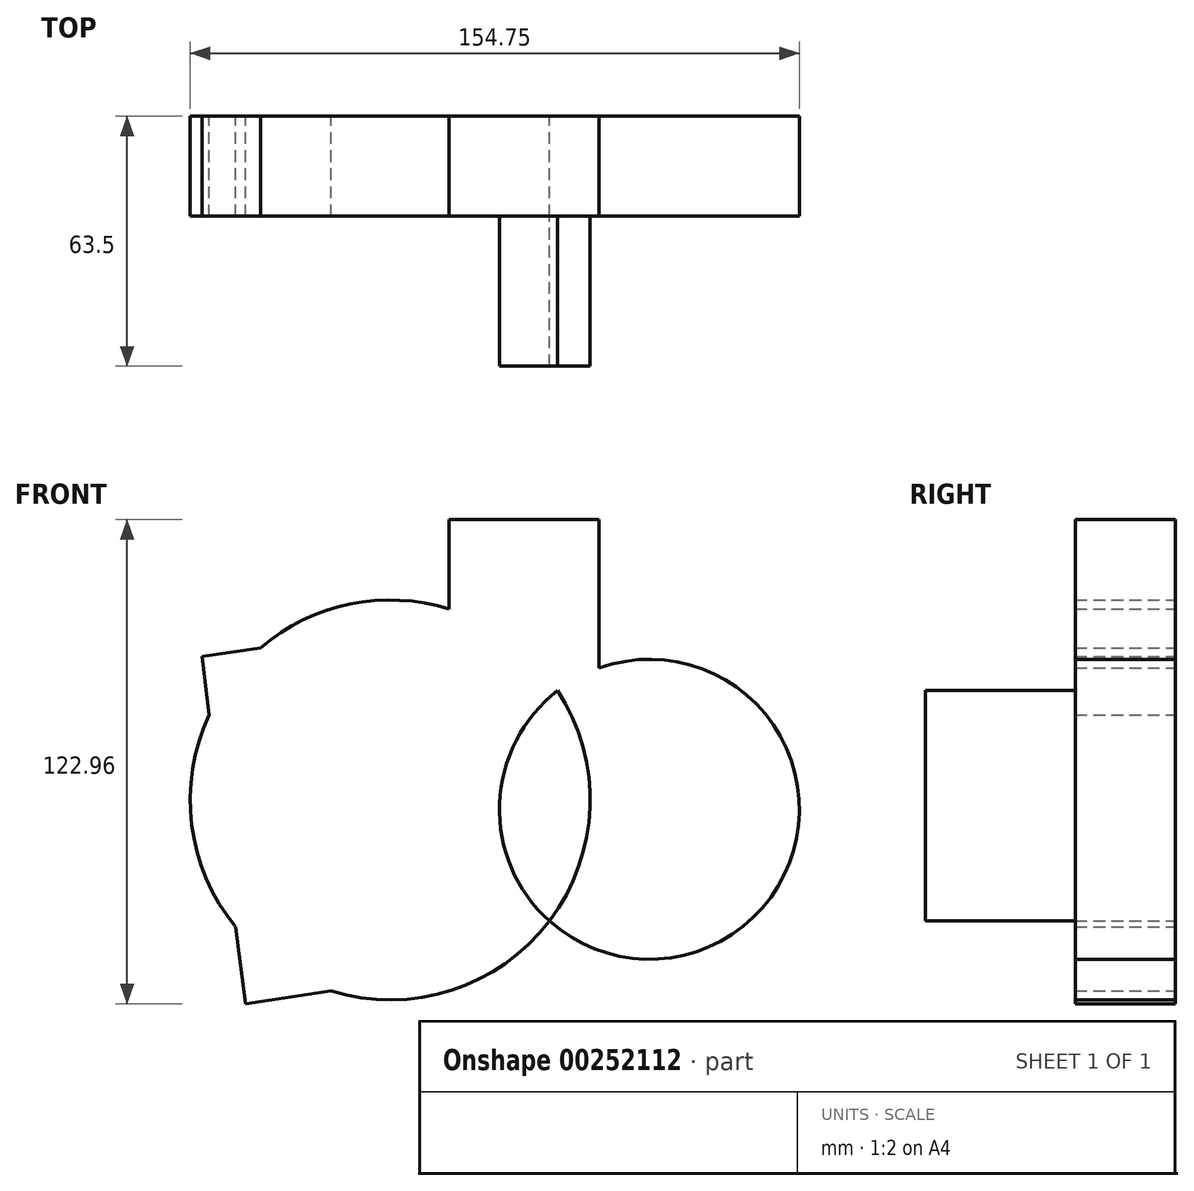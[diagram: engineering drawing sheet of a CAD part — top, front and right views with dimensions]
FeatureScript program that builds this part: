
annotation { "Feature Type Name" : "Feature", "Feature Type Description" : "" }
export const myFeature = defineFeature(function(context is Context, id is Id, definition is map)
    precondition{}
    {
        {
            var Q0;
            Q0=qCreatedBy(makeId("Front.planeOp"),FACE);
            var sketch = newSketch(context, id + "F0", { "sketchPlane" : qUnion([Q0])});
            skCircle(sketch, "E0", {"center": v(0, 0) * mm, "radius": 38.1 * mm});
            skLineSegment(sketch, "E1", {"start": v(-12.75, 12.71) * mm, "end": v(-12.75, 73.57) * mm});
            skLineSegment(sketch, "E2", {"start": v(-12.75, 73.57) * mm, "end": v(-50.85, 73.57) * mm});
            skLineSegment(sketch, "E3", {"start": v(-50.85, 73.57) * mm, "end": v(-50.85, 48.17) * mm});
            skLineSegment(sketch, "E4", {"start": v(-50.85, 48.17) * mm, "end": v(-39.82, -40.04) * mm});
            skLineSegment(sketch, "E5", {"start": v(-50.85, 48.17) * mm, "end": v(-113.66, 38.82) * mm});
            skLineSegment(sketch, "E6", {"start": v(-113.66, 38.82) * mm, "end": v(-102.63, -49.4) * mm});
            skLineSegment(sketch, "E7", {"start": v(-102.63, -49.4) * mm, "end": v(-39.82, -40.04) * mm});
            skCircle(sketch, "E8", {"center": v(-65.85, 2.36) * mm, "radius": 50.8 * mm});
            skSolve(sketch);
        }
        {
            var Q0;
            {var subQ0=sQuery(id+"F0.wireOp",EDGE,"E8");var subQ1=sQuery(id+"F0.wireOp",EDGE,"E0");var subQ2=makeQuery(id+"F0.imprint","INTERSECT",VERTEX,{"disambiguationData":[OD(0.0)],"derivedFrom":[subQ1,subQ0]});Q0=makeQuery(id+"F0.imprint","IMPRINT",FACE,{"disambiguationData":[TD([[makeQuery(id+"F0.imprint","IMPRINT",EDGE,{"disambiguationData":[TD([[subQ2,1.0]])],"derivedFrom":subQ1}),1.0]])]});}
            extrude(context, id + "F1", {"entities" : qUnion([Q0]), "depth" : 63.5 * mm});
        }
        {
            var Q0;
            Q0 = qSketchRegion(id + "F0", true);
            extrude(context, id + "F2", {"entities" : qUnion([Q0]), "operationType" : NewBodyOperationType.ADD, "depth" : 25.4 * mm});
        }
    });
